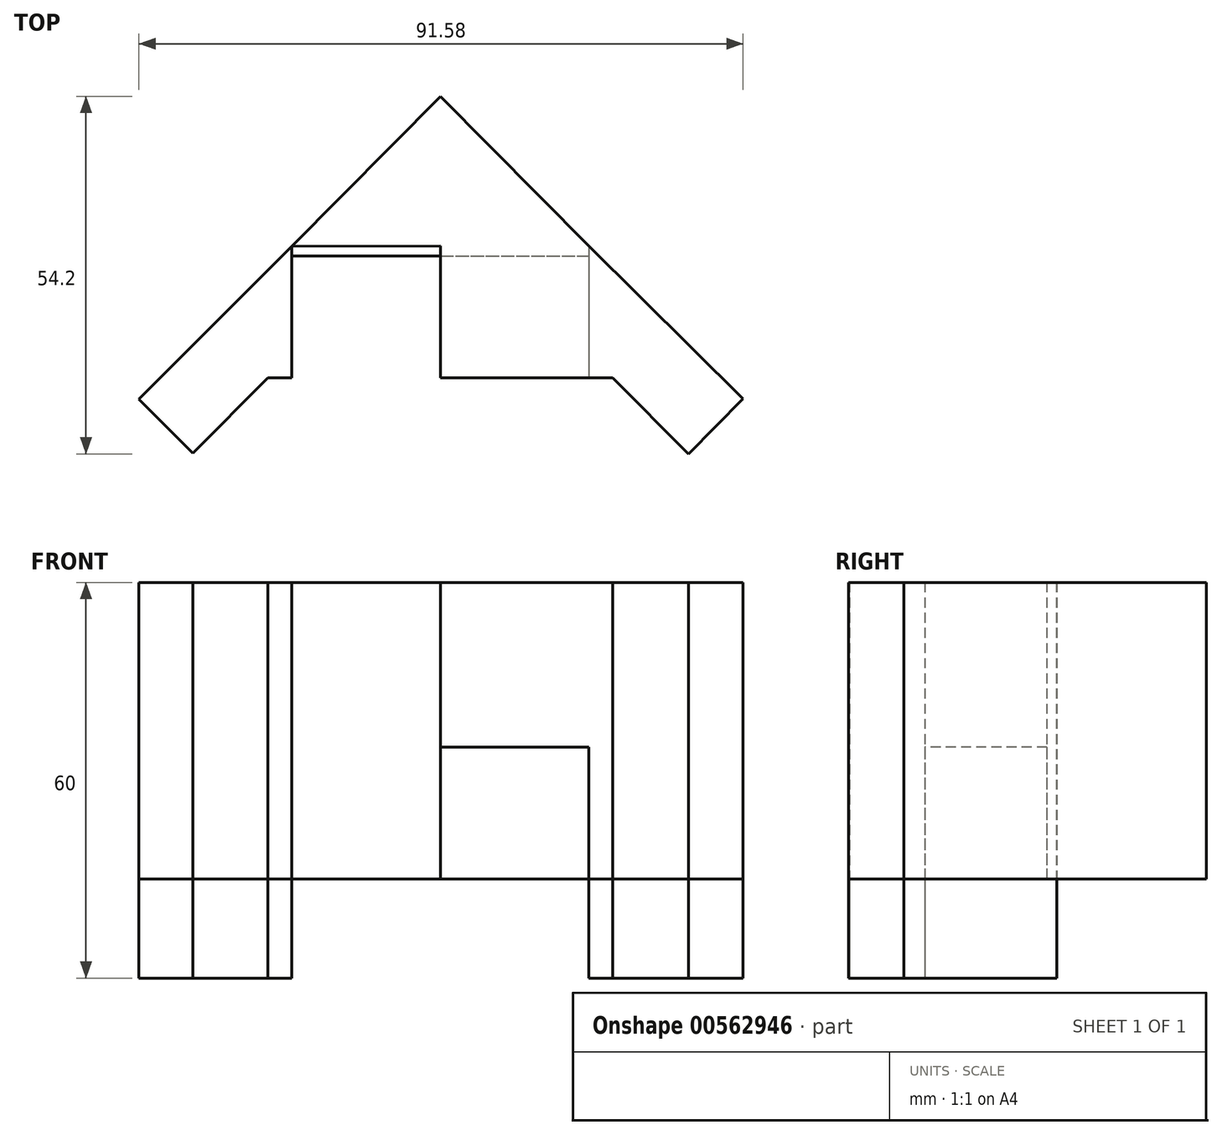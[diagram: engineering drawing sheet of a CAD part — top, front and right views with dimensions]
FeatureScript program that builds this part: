
annotation { "Feature Type Name" : "Feature", "Feature Type Description" : "" }
export const myFeature = defineFeature(function(context is Context, id is Id, definition is map)
    precondition{}
    {
        {
            var Q0;
            Q0=qCreatedBy(makeId("Top.planeOp"),FACE);
            var sketch = newSketch(context, id + "F0", { "sketchPlane" : qUnion([Q0])});
            skCircle(sketch, "E0", {"center": v(-0.03, 1.02) * mm, "radius": 105 * mm});
            skCircle(sketch, "E1", {"center": v(-29.75, 90.8) * mm, "radius": 6.5 * mm});
            skCircle(sketch, "E2", {"center": v(29.27, 90.8) * mm, "radius": 6.5 * mm});
            skCircle(sketch, "E3", {"center": v(-91.34, -22.45) * mm, "radius": 6.5 * mm});
            skCircle(sketch, "E4", {"center": v(91.29, -22.45) * mm, "radius": 6.5 * mm});
            skLineSegment(sketch, "E5", {"start": v(-26.15, -74.78) * mm, "end": v(26.1, -74.78) * mm});
            skLineSegment(sketch, "E6", {"start": v(-26.15, -74.78) * mm, "end": v(-45.16, -93.79) * mm});
            skLineSegment(sketch, "E7", {"start": v(26.1, -74.78) * mm, "end": v(45.1, -93.79) * mm});
            skLineSegment(sketch, "E8", {"start": v(0, 0) * mm, "end": v(104.97, 0) * mm});
            skLineSegment(sketch, "E9.left", {"start": v(0, 0) * mm, "end": v(0, 103.03) * mm});
            skLineSegment(sketch, "E10.left", {"start": v(0, 0) * mm, "end": v(0, 104.98) * mm});
            skLineSegment(sketch, "E11", {"start": v(-20.96, 21.1) * mm, "end": v(-32.26, 9.77) * mm});
            skLineSegment(sketch, "E12", {"start": v(-20.96, 21.1) * mm, "end": v(-9.66, 32.42) * mm});
            skLineSegment(sketch, "E13", {"start": v(21, 21) * mm, "end": v(9.68, 32.31) * mm});
            skLineSegment(sketch, "E14", {"start": v(9.68, 32.31) * mm, "end": v(32.31, 9.68) * mm});
            skLineSegment(sketch, "E15", {"start": v(-20, -20) * mm, "end": v(-31.32, -8.7) * mm});
            skLineSegment(sketch, "E16", {"start": v(-20, -20) * mm, "end": v(-8.7, -31.32) * mm});
            skLineSegment(sketch, "E17", {"start": v(20.08, -19.9) * mm, "end": v(31.34, -8.52) * mm});
            skLineSegment(sketch, "E18", {"start": v(31.34, -8.52) * mm, "end": v(20.08, -19.9) * mm});
            skLineSegment(sketch, "E19", {"start": v(20.08, -19.9) * mm, "end": v(8.82, -31.26) * mm});
            skLineSegment(sketch, "E20", {"start": v(-0.03, 1.02) * mm, "end": v(0, -74.78) * mm});
            skLineSegment(sketch, "E21.bottom", {"start": v(-82.14, 0) * mm, "end": v(-68.14, 0) * mm});
            skLineSegment(sketch, "E21.top", {"start": v(-82.14, 20) * mm, "end": v(-68.14, 20) * mm});
            skLineSegment(sketch, "E21.left", {"start": v(-85.14, 3) * mm, "end": v(-85.14, 17) * mm});
            skLineSegment(sketch, "E21.right", {"start": v(-65.14, 3) * mm, "end": v(-65.14, 17) * mm});
            skLineSegment(sketch, "E22.bottom", {"start": v(82.1, 0) * mm, "end": v(68.1, 0) * mm});
            skLineSegment(sketch, "E22.top", {"start": v(82.1, 20) * mm, "end": v(68.1, 20) * mm});
            skLineSegment(sketch, "E22.left", {"start": v(85.1, 3) * mm, "end": v(85.1, 17) * mm});
            skLineSegment(sketch, "E22.right", {"start": v(65.1, 3) * mm, "end": v(65.1, 17) * mm});
            skPoint(sketch, "E23.visualSharp", {"position": v(-85.14, 20) * mm});
            skArc(sketch, "E23.filletArc", {"start": v(-82.14, 20) * mm, "mid": v(-84.26, 19.12) * mm, "end": v(-85.14, 17) * mm});
            skPoint(sketch, "E24.visualSharp", {"position": v(-65.14, 20) * mm});
            skArc(sketch, "E24.filletArc", {"start": v(-65.14, 17) * mm, "mid": v(-66.01, 19.12) * mm, "end": v(-68.14, 20) * mm});
            skPoint(sketch, "E25.visualSharp", {"position": v(-65.14, 0) * mm});
            skArc(sketch, "E25.filletArc", {"start": v(-68.14, 0) * mm, "mid": v(-66.01, 0.88) * mm, "end": v(-65.14, 3) * mm});
            skPoint(sketch, "E26.visualSharp", {"position": v(-85.14, 0) * mm});
            skArc(sketch, "E26.filletArc", {"start": v(-85.14, 3) * mm, "mid": v(-84.26, 0.88) * mm, "end": v(-82.14, 0) * mm});
            skPoint(sketch, "E27.visualSharp", {"position": v(65.1, 0) * mm});
            skArc(sketch, "E27.filletArc", {"start": v(65.1, 3) * mm, "mid": v(65.98, 0.88) * mm, "end": v(68.1, 0) * mm});
            skPoint(sketch, "E28.visualSharp", {"position": v(65.1, 20) * mm});
            skArc(sketch, "E28.filletArc", {"start": v(68.1, 20) * mm, "mid": v(65.98, 19.12) * mm, "end": v(65.1, 17) * mm});
            skPoint(sketch, "E29.visualSharp", {"position": v(85.1, 20) * mm});
            skArc(sketch, "E29.filletArc", {"start": v(85.1, 17) * mm, "mid": v(84.23, 19.12) * mm, "end": v(82.1, 20) * mm});
            skPoint(sketch, "E30.visualSharp", {"position": v(85.1, 0) * mm});
            skArc(sketch, "E30.filletArc", {"start": v(82.1, 0) * mm, "mid": v(84.23, 0.88) * mm, "end": v(85.1, 3) * mm});
            skLineSegment(sketch, "E31", {"start": v(50.85, -72.9) * mm, "end": v(37.6, -86.28) * mm});
            skLineSegment(sketch, "E32", {"start": v(73.53, -50.31) * mm, "end": v(87.6, -36.1) * mm});
            skLineSegment(sketch, "E33", {"start": v(87.6, -36.1) * mm, "end": v(95.07, -43.5) * mm});
            skLineSegment(sketch, "E34", {"start": v(50.85, -72.9) * mm, "end": v(8.82, -31.26) * mm});
            skLineSegment(sketch, "E35", {"start": v(31.34, -8.52) * mm, "end": v(73.53, -50.31) * mm});
            skLineSegment(sketch, "E36", {"start": v(-50.53, -73.16) * mm, "end": v(-37.53, -86.16) * mm});
            skLineSegment(sketch, "E37", {"start": v(-73.32, -50.69) * mm, "end": v(-87.46, -36.55) * mm});
            skLineSegment(sketch, "E38", {"start": v(-87.46, -36.55) * mm, "end": v(-94.9, -43.98) * mm});
            skLineSegment(sketch, "E39", {"start": v(-73.32, -50.69) * mm, "end": v(-31.32, -8.7) * mm});
            skLineSegment(sketch, "E40", {"start": v(-8.7, -31.32) * mm, "end": v(-50.53, -73.16) * mm});
            skLineSegment(sketch, "E41", {"start": v(-74.16, 51.56) * mm, "end": v(-88.28, 37.4) * mm});
            skLineSegment(sketch, "E42", {"start": v(-88.28, 37.4) * mm, "end": v(-95.54, 44.64) * mm});
            skLineSegment(sketch, "E43", {"start": v(-51.69, 74.34) * mm, "end": v(-37.56, 88.5) * mm});
            skLineSegment(sketch, "E44", {"start": v(-37.56, 88.5) * mm, "end": v(-44.98, 95.9) * mm});
            skLineSegment(sketch, "E45", {"start": v(-51.69, 74.34) * mm, "end": v(-9.66, 32.42) * mm});
            skLineSegment(sketch, "E46", {"start": v(-74.16, 51.56) * mm, "end": v(-32.26, 9.77) * mm});
            skLineSegment(sketch, "E47", {"start": v(51.68, 74.3) * mm, "end": v(37.54, 88.45) * mm});
            skPoint(sketch, "E48.endSnap0", {"position": v(44.6, 81.38) * mm});
            skPoint(sketch, "E49.endSnap0", {"position": v(0, 51.52) * mm});
            skLineSegment(sketch, "E50", {"start": v(74.14, 51.52) * mm, "end": v(88.29, 37.38) * mm});
            skLineSegment(sketch, "E51", {"start": v(51.68, 74.3) * mm, "end": v(9.68, 32.31) * mm});
            skLineSegment(sketch, "E52", {"start": v(74.14, 51.52) * mm, "end": v(32.31, 9.68) * mm});
            skLineSegment(sketch, "E53", {"start": v(0, 74.3) * mm, "end": v(7, 74.3) * mm});
            skLineSegment(sketch, "E54", {"start": v(10, 71.3) * mm, "end": v(10, 57.3) * mm});
            skLineSegment(sketch, "E55", {"start": v(7, 54.3) * mm, "end": v(-7, 54.3) * mm});
            skLineSegment(sketch, "E56", {"start": v(-10, 57.3) * mm, "end": v(-10, 71.3) * mm});
            skLineSegment(sketch, "E57", {"start": v(-7, 74.3) * mm, "end": v(0, 74.3) * mm});
            skPoint(sketch, "E58.visualSharp", {"position": v(-10, 74.3) * mm});
            skArc(sketch, "E58.filletArc", {"start": v(-7, 74.3) * mm, "mid": v(-9.12, 73.43) * mm, "end": v(-10, 71.3) * mm});
            skPoint(sketch, "E59.visualSharp", {"position": v(10, 74.3) * mm});
            skArc(sketch, "E59.filletArc", {"start": v(10, 71.3) * mm, "mid": v(9.12, 73.43) * mm, "end": v(7, 74.3) * mm});
            skPoint(sketch, "E60.visualSharp", {"position": v(10, 54.3) * mm});
            skArc(sketch, "E60.filletArc", {"start": v(7, 54.3) * mm, "mid": v(9.12, 55.18) * mm, "end": v(10, 57.3) * mm});
            skPoint(sketch, "E61.visualSharp", {"position": v(-10, 54.3) * mm});
            skArc(sketch, "E61.filletArc", {"start": v(-10, 57.3) * mm, "mid": v(-9.12, 55.18) * mm, "end": v(-7, 54.3) * mm});
            skLineSegment(sketch, "E62", {"start": v(32.31, 9.68) * mm, "end": v(74.14, 51.52) * mm});
            skLineSegment(sketch, "E63", {"start": v(88.29, 37.38) * mm, "end": v(95.5, 44.6) * mm});
            skLineSegment(sketch, "E64", {"start": v(37.54, 88.45) * mm, "end": v(44.97, 95.88) * mm});
            skLineSegment(sketch, "E65", {"start": v(0, -74.78) * mm, "end": v(-22.5, -74.78) * mm});
            skLineSegment(sketch, "E66", {"start": v(-22.5, -74.78) * mm, "end": v(-22.5, -54.78) * mm});
            skLineSegment(sketch, "E67", {"start": v(-22.5, -54.78) * mm, "end": v(22.5, -54.76) * mm});
            skLineSegment(sketch, "E68", {"start": v(22.5, -54.76) * mm, "end": v(22.5, -74.78) * mm});
            skLineSegment(sketch, "E69", {"start": v(22.5, -54.76) * mm, "end": v(45.88, -77.92) * mm});
            skLineSegment(sketch, "E70", {"start": v(-22.5, -54.78) * mm, "end": v(-45.7, -77.98) * mm});
            skLineSegment(sketch, "E71", {"start": v(-22.5, -54.78) * mm, "end": v(-0.02, -32.08) * mm});
            skLineSegment(sketch, "E72", {"start": v(-0.02, -32.08) * mm, "end": v(22.5, -54.76) * mm});
            skLineSegment(sketch, "E73", {"start": v(-22.5, -56.24) * mm, "end": v(22.5, -56.24) * mm});
            skSolve(sketch);
        }
        {
            var Q0;
            {var subQ0=sQuery(id+"F0.wireOp",EDGE,"E66");Q0=makeQuery(id+"F0.imprint","IMPRINT",FACE,{"disambiguationData":[TD([[makeQuery(id+"F0.imprint","IMPRINT",EDGE,{"derivedFrom":subQ0}),1.0]])]});}
            var Q1;
            {var subQ0=sQuery(id+"F0.wireOp",EDGE,"E68");Q1=makeQuery(id+"F0.imprint","IMPRINT",FACE,{"disambiguationData":[TD([[makeQuery(id+"F0.imprint","IMPRINT",EDGE,{"derivedFrom":subQ0}),1.0]])]});}
            extrude(context, id + "F1", {"entities" : qUnion([Q0, Q1]), "depth" : 15 * mm, "offsetDistance" : 25.4 * mm});
        }
        {
            var Q0;
            {var subQ0=sQuery(id+"F0.wireOp",EDGE,"E65");Q0=makeQuery(id+"F0.imprint","IMPRINT",FACE,{"disambiguationData":[TD([[makeQuery(id+"F0.imprint","IMPRINT",EDGE,{"derivedFrom":subQ0}),-1.0]])]});}
            var Q1;
            {var subQ3=sQuery(id+"F0.wireOp",EDGE,"E68");Q1=makeQuery(id+"F0.imprint","IMPRINT",FACE,{"disambiguationData":[TD([[makeQuery(id+"F0.imprint","IMPRINT",EDGE,{"derivedFrom":subQ3}),-1.0]])]});}
            var Q2;
            {var subQ6=sQuery(id+"F0.wireOp",EDGE,"E68");Q2=makeQuery(id+"F0.imprint","IMPRINT",FACE,{"disambiguationData":[TD([[makeQuery(id+"F0.imprint","IMPRINT",EDGE,{"derivedFrom":subQ6}),1.0]])]});}
            var Q3;
            {var subQ0=sQuery(id+"F0.wireOp",EDGE,"E72");Q3=makeQuery(id+"F0.imprint","IMPRINT",FACE,{"disambiguationData":[TD([[makeQuery(id+"F0.imprint","IMPRINT",EDGE,{"derivedFrom":subQ0}),-1.0]])]});}
            var Q4;
            {var subQ0=sQuery(id+"F0.wireOp",EDGE,"E71");Q4=makeQuery(id+"F0.imprint","IMPRINT",FACE,{"disambiguationData":[TD([[makeQuery(id+"F0.imprint","IMPRINT",EDGE,{"derivedFrom":subQ0}),-1.0]])]});}
            var Q5;
            {var subQ0=sQuery(id+"F0.wireOp",EDGE,"E66");Q5=makeQuery(id+"F0.imprint","IMPRINT",FACE,{"disambiguationData":[TD([[makeQuery(id+"F0.imprint","IMPRINT",EDGE,{"derivedFrom":subQ0}),1.0]])]});}
            extrude(context, id + "F2", {"entities" : qUnion([Q0, Q1, Q2, Q3, Q4, Q5]), "depth" : 60 * mm, "offsetDistance" : 25.4 * mm});
        }
        {
            var Q0;
            {var subQ8=sQuery(id+"F0.wireOp",EDGE,"E70");Q0=makeQuery(id+"F0.imprint","IMPRINT",FACE,{"disambiguationData":[TD([[makeQuery(id+"F0.imprint","IMPRINT",EDGE,{"derivedFrom":subQ8}),1.0]])]});}
            var Q1;
            {var subQ0=sQuery(id+"F0.wireOp",EDGE,"E65");Q1=makeQuery(id+"F0.imprint","IMPRINT",FACE,{"disambiguationData":[TD([[makeQuery(id+"F0.imprint","IMPRINT",EDGE,{"derivedFrom":subQ0}),-1.0]])]});}
            var Q2;
            {var subQ1=sQuery(id+"F0.wireOp",EDGE,"E5");var subQ3=sQuery(id+"F0.wireOp",EDGE,"E68");var subQ4=makeQuery(id+"F0.imprint","INTERSECT",VERTEX,{"derivedFrom":[subQ1,subQ3]});Q2=makeQuery(id+"F0.imprint","IMPRINT",FACE,{"disambiguationData":[TD([[makeQuery(id+"F0.imprint","IMPRINT",EDGE,{"disambiguationData":[TD([[subQ4,1.0]])],"derivedFrom":subQ3}),-1.0]])]});}
            var Q3;
            {var subQ0=sQuery(id+"F0.wireOp",EDGE,"E69");Q3=makeQuery(id+"F0.imprint","IMPRINT",FACE,{"disambiguationData":[TD([[makeQuery(id+"F0.imprint","IMPRINT",EDGE,{"derivedFrom":subQ0}),-1.0]])]});}
            var Q4;
            {var subQ0=sQuery(id+"F0.wireOp",EDGE,"E67");var subQ1=sQuery(id+"F0.wireOp",EDGE,"E20");var subQ2=makeQuery(id+"F0.imprint","INTERSECT",VERTEX,{"derivedFrom":[subQ1,subQ0]});Q4=makeQuery(id+"F0.imprint","IMPRINT",FACE,{"disambiguationData":[TD([[makeQuery(id+"F0.imprint","IMPRINT",EDGE,{"disambiguationData":[TD([[subQ2,-1.0]])],"derivedFrom":subQ1}),-1.0]])]});}
            var Q5;
            {var subQ0=sQuery(id+"F0.wireOp",EDGE,"E67");var subQ1=sQuery(id+"F0.wireOp",EDGE,"E20");var subQ2=makeQuery(id+"F0.imprint","INTERSECT",VERTEX,{"derivedFrom":[subQ1,subQ0]});Q5=makeQuery(id+"F0.imprint","IMPRINT",FACE,{"disambiguationData":[TD([[makeQuery(id+"F0.imprint","IMPRINT",EDGE,{"disambiguationData":[TD([[subQ2,-1.0]])],"derivedFrom":subQ1}),1.0]])]});}
            var Q6;
            {var subQ0=sQuery(id+"F0.wireOp",EDGE,"E71");Q6=makeQuery(id+"F0.imprint","IMPRINT",FACE,{"disambiguationData":[TD([[makeQuery(id+"F0.imprint","IMPRINT",EDGE,{"derivedFrom":subQ0}),-1.0]])]});}
            var Q7;
            {var subQ0=sQuery(id+"F0.wireOp",EDGE,"E72");Q7=makeQuery(id+"F0.imprint","IMPRINT",FACE,{"disambiguationData":[TD([[makeQuery(id+"F0.imprint","IMPRINT",EDGE,{"derivedFrom":subQ0}),-1.0]])]});}
            extrude(context, id + "F3", {"entities" : qUnion([Q0, Q1, Q2, Q3, Q4, Q5, Q6, Q7]), "depth" : 60 * mm, "offsetDistance" : 25.4 * mm});
        }
        {
            var Q0;
            {var subQ0=sQuery(id+"F0.wireOp",EDGE,"E65");Q0=makeQuery(id+"F0.imprint","IMPRINT",FACE,{"disambiguationData":[TD([[makeQuery(id+"F0.imprint","IMPRINT",EDGE,{"derivedFrom":subQ0}),-1.0]])]});}
            var Q1;
            {var subQ1=sQuery(id+"F0.wireOp",EDGE,"E5");var subQ3=sQuery(id+"F0.wireOp",EDGE,"E68");var subQ4=makeQuery(id+"F0.imprint","INTERSECT",VERTEX,{"derivedFrom":[subQ1,subQ3]});Q1=makeQuery(id+"F0.imprint","IMPRINT",FACE,{"disambiguationData":[TD([[makeQuery(id+"F0.imprint","IMPRINT",EDGE,{"disambiguationData":[TD([[subQ4,1.0]])],"derivedFrom":subQ3}),-1.0]])]});}
            extrude(context, id + "F4", {"entities" : qUnion([Q0, Q1]), "operationType" : NewBodyOperationType.REMOVE, "depth" : 35 * mm, "offsetDistance" : 25.4 * mm});
        }
        {
            var Q0;
            {var subQ0=sQuery(id+"F0.wireOp",EDGE,"E67");var subQ1=sQuery(id+"F0.wireOp",EDGE,"E20");var subQ2=makeQuery(id+"F0.imprint","INTERSECT",VERTEX,{"derivedFrom":[subQ1,subQ0]});Q0=makeQuery(id+"F0.imprint","IMPRINT",FACE,{"disambiguationData":[TD([[makeQuery(id+"F0.imprint","IMPRINT",EDGE,{"disambiguationData":[TD([[subQ2,-1.0]])],"derivedFrom":subQ1}),-1.0]])]});}
            var Q1;
            {var subQ0=sQuery(id+"F0.wireOp",EDGE,"E67");var subQ1=sQuery(id+"F0.wireOp",EDGE,"E20");var subQ2=makeQuery(id+"F0.imprint","INTERSECT",VERTEX,{"derivedFrom":[subQ1,subQ0]});Q1=makeQuery(id+"F0.imprint","IMPRINT",FACE,{"disambiguationData":[TD([[makeQuery(id+"F0.imprint","IMPRINT",EDGE,{"disambiguationData":[TD([[subQ2,-1.0]])],"derivedFrom":subQ1}),1.0]])]});}
            var Q2;
            {var subQ0=sQuery(id+"F0.wireOp",EDGE,"E72");Q2=makeQuery(id+"F0.imprint","IMPRINT",FACE,{"disambiguationData":[TD([[makeQuery(id+"F0.imprint","IMPRINT",EDGE,{"derivedFrom":subQ0}),-1.0]])]});}
            var Q3;
            {var subQ0=sQuery(id+"F0.wireOp",EDGE,"E71");Q3=makeQuery(id+"F0.imprint","IMPRINT",FACE,{"disambiguationData":[TD([[makeQuery(id+"F0.imprint","IMPRINT",EDGE,{"derivedFrom":subQ0}),-1.0]])]});}
            extrude(context, id + "F5", {"entities" : qUnion([Q0, Q1, Q2, Q3]), "operationType" : NewBodyOperationType.REMOVE, "depth" : 15 * mm, "offsetDistance" : 25.4 * mm});
        }
    });
